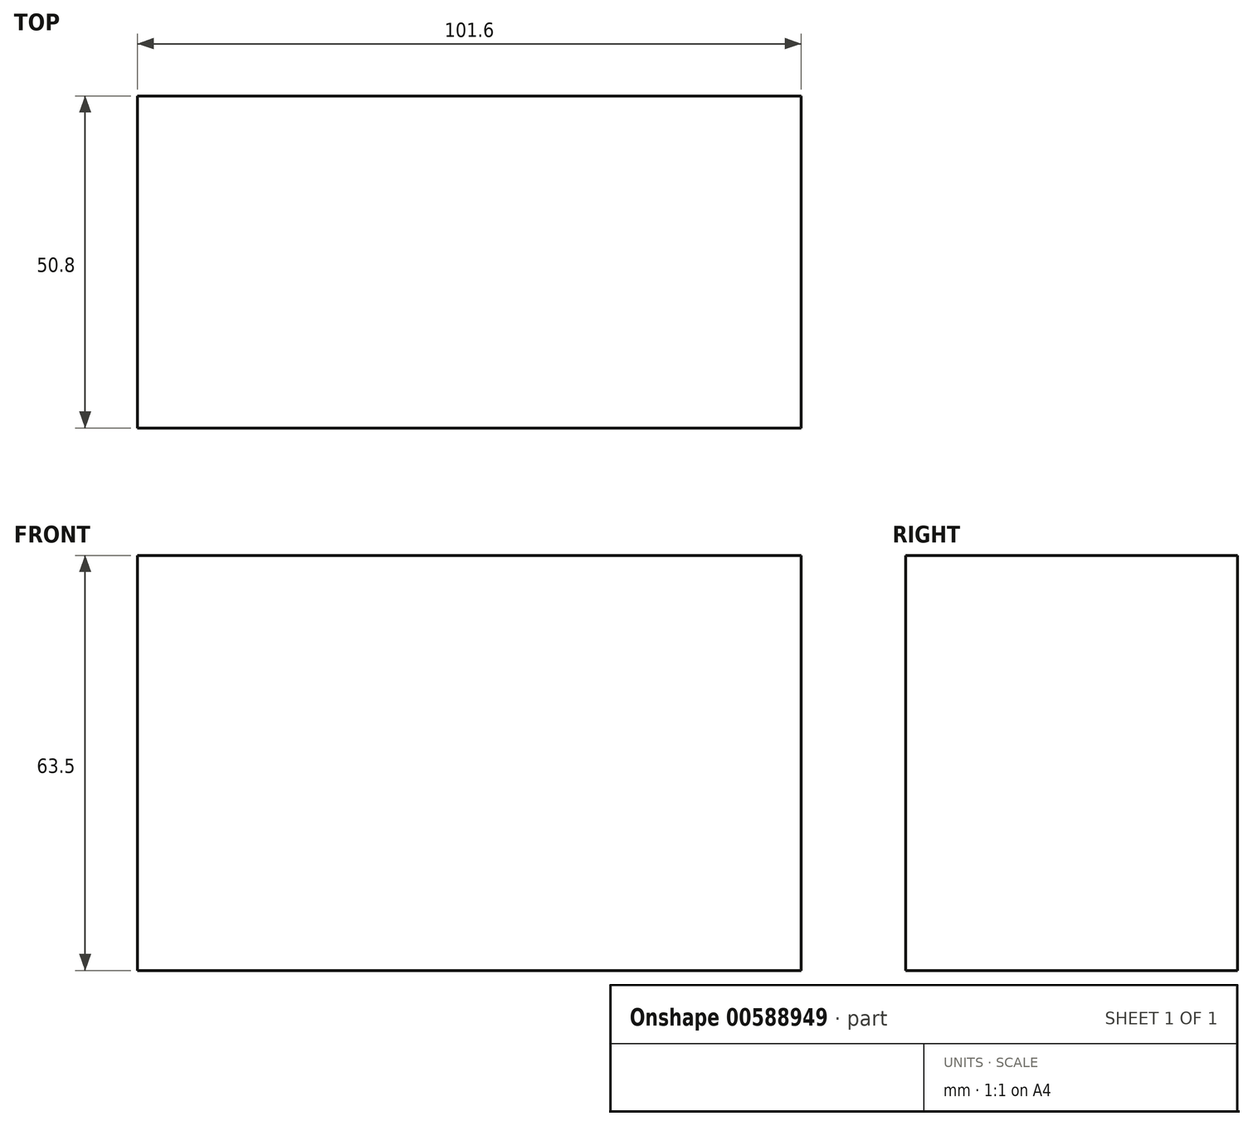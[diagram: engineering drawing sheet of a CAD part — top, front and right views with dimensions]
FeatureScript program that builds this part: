
annotation { "Feature Type Name" : "Feature", "Feature Type Description" : "" }
export const myFeature = defineFeature(function(context is Context, id is Id, definition is map)
    precondition{}
    {
        {
            var Q0;
            Q0=qCreatedBy(makeId("Front.planeOp"),FACE);
            var sketch = newSketch(context, id + "F0", { "sketchPlane" : qUnion([Q0])});
            skLineSegment(sketch, "E0.bottom", {"start": v(-50.8, 31.75) * mm, "end": v(50.8, 31.75) * mm});
            skLineSegment(sketch, "E0.top", {"start": v(-50.8, -31.75) * mm, "end": v(50.8, -31.75) * mm});
            skLineSegment(sketch, "E0.left", {"start": v(-50.8, 31.75) * mm, "end": v(-50.8, -31.75) * mm});
            skLineSegment(sketch, "E0.right", {"start": v(50.8, 31.75) * mm, "end": v(50.8, -31.75) * mm});
            skSolve(sketch);
        }
        {
            var Q0;
            Q0=makeQuery(id+"F0.imprint","IMPRINT",FACE,{"disambiguationData":[TD([[makeQuery(id+"F0.imprint","IMPRINT",EDGE,{"derivedFrom":sQuery(id+"F0.wireOp",EDGE,"E0.bottom")}),-1.0]])]});
            extrude(context, id + "F1", {"entities" : qUnion([Q0]), "depth" : 25.4 * mm, "offsetDistance" : 25.4 * mm, "hasSecondDirection" : true, "secondDirectionOppositeDirection" : true, "secondDirectionDepth" : 25.4 * mm});
        }
    });
